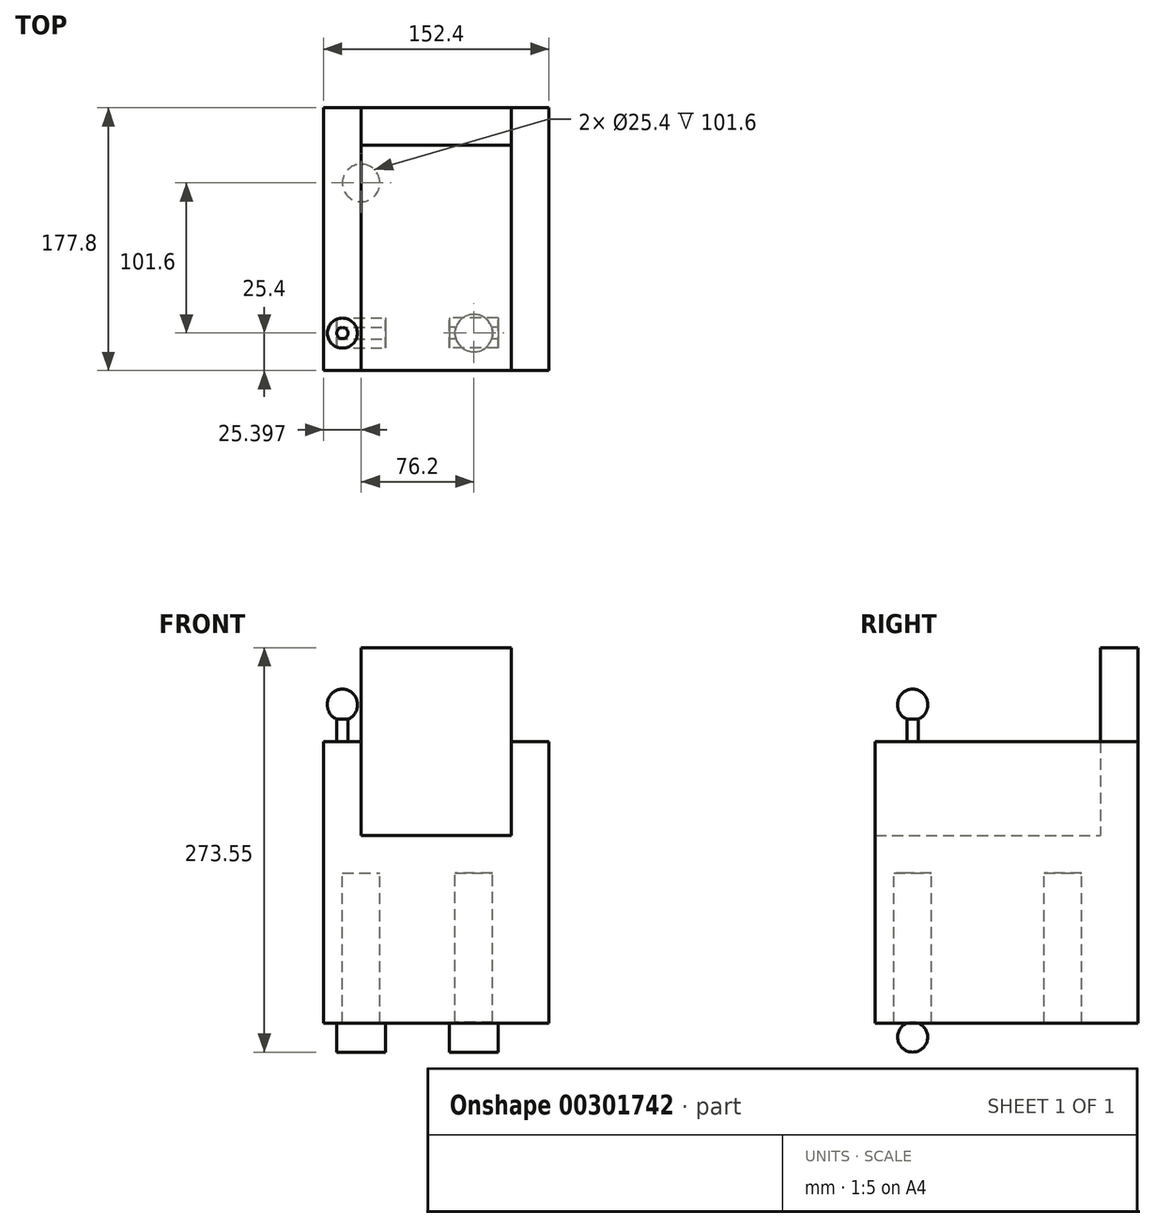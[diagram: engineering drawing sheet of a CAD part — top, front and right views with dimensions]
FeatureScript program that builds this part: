
annotation { "Feature Type Name" : "Feature", "Feature Type Description" : "" }
export const myFeature = defineFeature(function(context is Context, id is Id, definition is map)
    precondition{}
    {
        {
            var Q0;
            Q0=qCreatedBy(makeId("Front.planeOp"),FACE);
            var sketch = newSketch(context, id + "F0", { "sketchPlane" : qUnion([Q0])});
            skLineSegment(sketch, "E0.bottom", {"start": v(-64.76, 10.66) * mm, "end": v(62.24, 10.66) * mm});
            skLineSegment(sketch, "E0.top", {"start": v(-64.76, -14.74) * mm, "end": v(62.24, -14.74) * mm});
            skLineSegment(sketch, "E0.left", {"start": v(-64.76, 10.66) * mm, "end": v(-64.76, -14.74) * mm});
            skLineSegment(sketch, "E0.right", {"start": v(62.24, 10.66) * mm, "end": v(62.24, -14.74) * mm});
            skSolve(sketch);
        }
        {
            var Q0;
            Q0=makeQuery(id+"F0.imprint","IMPRINT",FACE,{"disambiguationData":[TD([[makeQuery(id+"F0.imprint","IMPRINT",EDGE,{"derivedFrom":sQuery(id+"F0.wireOp",EDGE,"E0.bottom")}),-1.0]])]});
            extrude(context, id + "F1", {"entities" : qUnion([Q0]), "endBound" : BoundingType.SYMMETRIC, "depth" : 152.4 * mm});
        }
        {
            var Q0;
            Q0=makeQuery(id+"F1.opExtrude","SWEPT_FACE",FACE,{"disambiguationData":[OSD([sQuery(id+"F0.wireOp",EDGE,"E0.top")])]});
            var sketch = newSketch(context, id + "F2", { "sketchPlane" : qUnion([Q0])});
            skCircle(sketch, "E1", {"center": v(-39.36, 50.8) * mm, "radius": 12.7 * mm});
            skLineSegment(sketch, "E2", {"start": v(-1.26, 76.2) * mm, "end": v(-1.26, -76.2) * mm, "construction": true});
            skLineSegment(sketch, "E3", {"start": v(-64.76, 0) * mm, "end": v(62.24, 0) * mm, "construction": true});
            skCircle(sketch, "E4.MirrorC", {"center": v(36.84, 50.8) * mm, "radius": 12.7 * mm});
            skLineSegment(sketch, "E5.MirrorCS", {"start": v(62.24, 0) * mm, "end": v(-64.76, 0) * mm, "construction": true});
            skCircle(sketch, "E6.MirrorC", {"center": v(-39.36, -50.8) * mm, "radius": 12.7 * mm});
            skCircle(sketch, "E7.MirrorC", {"center": v(36.84, -50.8) * mm, "radius": 12.7 * mm});
            skSolve(sketch);
        }
        {
            var Q0;
            Q0=makeQuery(id+"F2.imprint","IMPRINT",FACE,{"disambiguationData":[TD([[makeQuery(id+"F2.imprint","IMPRINT",EDGE,{"derivedFrom":sQuery(id+"F2.wireOp",EDGE,"E1")}),1.0]])]});
            var Q1;
            Q1=makeQuery(id+"F2.imprint","IMPRINT",FACE,{"disambiguationData":[TD([[makeQuery(id+"F2.imprint","IMPRINT",EDGE,{"derivedFrom":sQuery(id+"F2.wireOp",EDGE,"E4.MirrorC")}),-1.0]])]});
            var Q2;
            Q2=makeQuery(id+"F2.imprint","IMPRINT",FACE,{"disambiguationData":[TD([[makeQuery(id+"F2.imprint","IMPRINT",EDGE,{"derivedFrom":sQuery(id+"F2.wireOp",EDGE,"E7.MirrorC")}),1.0]])]});
            var Q3;
            Q3=makeQuery(id+"F2.imprint","IMPRINT",FACE,{"disambiguationData":[TD([[makeQuery(id+"F2.imprint","IMPRINT",EDGE,{"derivedFrom":sQuery(id+"F2.wireOp",EDGE,"E6.MirrorC")}),-1.0]])]});
            extrude(context, id + "F3", {"entities" : qUnion([Q0, Q1, Q2, Q3]), "operationType" : NewBodyOperationType.ADD, "depth" : 101.6 * mm});
        }
        {
            var Q0;
            Q0=qCreatedBy(makeId("Right.planeOp"),FACE);
            var sketch = newSketch(context, id + "F4", { "sketchPlane" : qUnion([Q0])});
            skCircle(sketch, "E8", {"center": v(-50.8, -125.73) * mm, "radius": 10.16 * mm});
            skLineSegment(sketch, "E9", {"start": v(0, 0) * mm, "end": v(0, -174.12) * mm, "construction": true});
            skCircle(sketch, "E10.MirrorC", {"center": v(50.8, -125.73) * mm, "radius": 10.16 * mm});
            skSolve(sketch);
        }
        {
            var Q0;
            Q0=makeQuery(id+"F4.imprint","IMPRINT",FACE,{"disambiguationData":[TD([[makeQuery(id+"F4.imprint","IMPRINT",EDGE,{"derivedFrom":sQuery(id+"F4.wireOp",EDGE,"E8")}),1.0]])]});
            var Q1;
            Q1=makeQuery(id+"F4.imprint","IMPRINT",FACE,{"disambiguationData":[TD([[makeQuery(id+"F4.imprint","IMPRINT",EDGE,{"derivedFrom":sQuery(id+"F4.wireOp",EDGE,"E10.MirrorC")}),-1.0]])]});
            extrude(context, id + "F5", {"entities" : qUnion([Q0, Q1]), "operationType" : NewBodyOperationType.ADD, "depth" : 53.34 * mm, "hasSecondDirection" : true, "secondDirectionOppositeDirection" : false, "secondDirectionDepth" : 20.32 * mm});
        }
        {
            var Q0;
            Q0=makeQuery(id+"F5.opExtrude","CAP_FACE",FACE,{"disambiguationData":[OSD([sQuery(id+"F4.wireOp",EDGE,"E10.MirrorC")])],"isStart":true});
            var Q1;
            Q1=makeQuery(id+"F5.opExtrude","CAP_FACE",FACE,{"disambiguationData":[OSD([sQuery(id+"F4.wireOp",EDGE,"E8")])],"isStart":true});
            extrude(context, id + "F6", {"entities" : qUnion([Q0, Q1]), "operationType" : NewBodyOperationType.ADD, "depth" : 76.2 * mm, "hasSecondDirection" : true, "secondDirectionOppositeDirection" : false, "secondDirectionDepth" : 43.18 * mm});
        }
        {
            var Q0;
            Q0=makeQuery(id+"F1.opExtrude","SWEPT_FACE",FACE,{"disambiguationData":[OSD([sQuery(id+"F0.wireOp",EDGE,"E0.right")])]});
            extrude(context, id + "F7", {"entities" : qUnion([Q0]), "operationType" : NewBodyOperationType.ADD, "depth" : 25.4 * mm});
        }
        {
            var Q0;
            {var subQ0=sQuery(id+"F0.wireOp",EDGE,"E0.bottom");Q0=makeQuery(id+"F7.boolean.opBoolean","MERGE",FACE,{"derivedFrom":[makeQuery(id+"F1.opExtrude","SWEPT_FACE",FACE,{"disambiguationData":[OSD([subQ0])]}),makeQuery(id+"F7.opExtrude","SWEPT_FACE",FACE,{"disambiguationData":[OSD([subQ0,sQuery(id+"F0.wireOp",EDGE,"E0.right")])]})]});}
            var sketch = newSketch(context, id + "F8", { "sketchPlane" : qUnion([Q0])});
            skLineSegment(sketch, "E11", {"start": v(62.24, -76.2) * mm, "end": v(62.24, 76.2) * mm});
            skLineSegment(sketch, "E12", {"start": v(11.44, -76.2) * mm, "end": v(11.44, 76.2) * mm, "construction": true});
            skLineSegment(sketch, "E13.MirrorCS", {"start": v(-39.36, -76.2) * mm, "end": v(-39.36, 76.2) * mm});
            skSolve(sketch);
        }
        {
            var Q0;
            {var subQ0=sQuery(id+"F8.wireOp",EDGE,"E11");Q0=makeQuery(id+"F8.imprint","IMPRINT",FACE,{"disambiguationData":[TD([[makeQuery(id+"F8.imprint","IMPRINT",EDGE,{"derivedFrom":subQ0}),-1.0]])]});}
            var Q1;
            {var subQ0=sQuery(id+"F8.wireOp",EDGE,"E13.MirrorCS");Q1=makeQuery(id+"F8.imprint","IMPRINT",FACE,{"disambiguationData":[TD([[makeQuery(id+"F8.imprint","IMPRINT",EDGE,{"derivedFrom":subQ0}),1.0]])]});}
            extrude(context, id + "F9", {"entities" : qUnion([Q0, Q1]), "operationType" : NewBodyOperationType.ADD, "depth" : 63.5 * mm});
        }
        {
            var Q0;
            {var subQ0=sQuery(id+"F0.wireOp",EDGE,"E0.right");var subQ1=sQuery(id+"F0.wireOp",EDGE,"E0.bottom");var subQ2=makeQuery(id+"F7.boolean.opBoolean","MERGE",EDGE,{"derivedFrom":[makeQuery(id+"F1.opExtrude","CAP_EDGE",EDGE,{"disambiguationData":[OSD([subQ1])],"isStart":true}),makeQuery(id+"F7.opExtrude","SWEPT_EDGE",EDGE,{"disambiguationData":[OSD([subQ1,subQ0]),TDD([makeQuery(id+"F1.opExtrude","CAP_VERTEX",VERTEX,{"disambiguationData":[OSD([subQ1,subQ0])],"isStart":true})])]})]});var subQ3=sQuery(id+"F0.wireOp",EDGE,"E0.left");Q0=makeQuery(id+"F9.boolean.opBoolean","MERGE",FACE,{"derivedFrom":[makeQuery(id+"F7.boolean.opBoolean","MERGE",FACE,{"derivedFrom":[makeQuery(id+"F1.opExtrude","CAP_FACE",FACE,{"disambiguationData":[OSD([subQ1,sQuery(id+"F0.wireOp",EDGE,"E0.top"),subQ3,subQ0])],"isStart":true}),makeQuery(id+"F7.opExtrude","SWEPT_FACE",FACE,{"disambiguationData":[OSD([subQ0]),TDD([makeQuery(id+"F1.opExtrude","CAP_EDGE",EDGE,{"disambiguationData":[OSD([subQ0])],"isStart":true})])]})]}),makeQuery(id+"F9.opExtrude","SWEPT_FACE",FACE,{"disambiguationData":[OSD([subQ1,subQ0]),TDD([makeQuery(id+"F8.imprint","IMPRINT",EDGE,{"disambiguationData":[TD([[makeQuery(id+"F8.imprint","INTERSECT",VERTEX,{"derivedFrom":[subQ2,sQuery(id+"F8.wireOp",EDGE,"E13.MirrorCS")]}),1.0]])],"derivedFrom":subQ2})])]}),makeQuery(id+"F9.opExtrude","SWEPT_FACE",FACE,{"disambiguationData":[OSD([subQ1,subQ0]),TDD([makeQuery(id+"F8.imprint","IMPRINT",EDGE,{"disambiguationData":[TD([[makeQuery(id+"F8.imprint","INTERSECT",VERTEX,{"derivedFrom":[subQ2,sQuery(id+"F8.wireOp",EDGE,"E11")]}),-1.0]])],"derivedFrom":subQ2})])]})]});}
            extrude(context, id + "F10", {"entities" : qUnion([Q0]), "operationType" : NewBodyOperationType.ADD, "depth" : 25.4 * mm});
        }
        {
            var Q0;
            {var subQ0=sQuery(id+"F0.wireOp",EDGE,"E0.right");var subQ1=sQuery(id+"F0.wireOp",EDGE,"E0.bottom");Q0=makeQuery(id+"F10.boolean.opBoolean","MERGE",FACE,{"derivedFrom":[makeQuery(id+"F7.boolean.opBoolean","MERGE",FACE,{"derivedFrom":[makeQuery(id+"F1.opExtrude","SWEPT_FACE",FACE,{"disambiguationData":[OSD([subQ1])]}),makeQuery(id+"F7.opExtrude","SWEPT_FACE",FACE,{"disambiguationData":[OSD([subQ1,subQ0])]})]}),makeQuery(id+"F10.opExtrude","SWEPT_FACE",FACE,{"disambiguationData":[OSD([subQ1,subQ0]),TDD([makeQuery(id+"F7.boolean.opBoolean","MERGE",EDGE,{"derivedFrom":[makeQuery(id+"F1.opExtrude","CAP_EDGE",EDGE,{"disambiguationData":[OSD([subQ1])],"isStart":true}),makeQuery(id+"F7.opExtrude","SWEPT_EDGE",EDGE,{"disambiguationData":[OSD([subQ1,subQ0]),TDD([makeQuery(id+"F1.opExtrude","CAP_VERTEX",VERTEX,{"disambiguationData":[OSD([subQ1,subQ0])],"isStart":true})])]})]})])]})]});}
            var sketch = newSketch(context, id + "F11", { "sketchPlane" : qUnion([Q0])});
            skLineSegment(sketch, "E14", {"start": v(-39.36, 76.2) * mm, "end": v(62.24, 76.2) * mm});
            skSolve(sketch);
        }
        {
            var Q0;
            Q0 = qSketchRegion(id + "F11", true);
            var Q1;
            {var subQ0=sQuery(id+"F11.wireOp",EDGE,"E14");Q1=makeQuery(id+"F11.imprint","IMPRINT",FACE,{"disambiguationData":[TD([[makeQuery(id+"F11.imprint","IMPRINT",EDGE,{"derivedFrom":subQ0}),1.0]])]});}
            extrude(context, id + "F12", {"entities" : qUnion([Q0, Q1]), "operationType" : NewBodyOperationType.ADD, "depth" : 127 * mm});
        }
        {
            var Q0;
            {var subQ0=sQuery(id+"F0.wireOp",EDGE,"E0.right");var subQ1=sQuery(id+"F0.wireOp",EDGE,"E0.bottom");var subQ2=makeQuery(id+"F7.boolean.opBoolean","MERGE",EDGE,{"derivedFrom":[makeQuery(id+"F1.opExtrude","CAP_EDGE",EDGE,{"disambiguationData":[OSD([subQ1])],"isStart":true}),makeQuery(id+"F7.opExtrude","SWEPT_EDGE",EDGE,{"disambiguationData":[OSD([subQ1,subQ0]),TDD([makeQuery(id+"F1.opExtrude","CAP_VERTEX",VERTEX,{"disambiguationData":[OSD([subQ1,subQ0])],"isStart":true})])]})]});var subQ3=sQuery(id+"F0.wireOp",EDGE,"E0.left");var subQ4=sQuery(id+"F8.wireOp",EDGE,"E13.MirrorCS");Q0=makeQuery(id+"F10.boolean.opBoolean","MERGE",FACE,{"derivedFrom":[makeQuery(id+"F9.opExtrude","CAP_FACE",FACE,{"disambiguationData":[OSD([subQ1,subQ3,subQ0,subQ4])],"isStart":false}),makeQuery(id+"F10.opExtrude","SWEPT_FACE",FACE,{"disambiguationData":[OSD([subQ1,subQ0]),TDD([makeQuery(id+"F9.opExtrude","CAP_EDGE",EDGE,{"disambiguationData":[OSD([subQ1,subQ0]),TDD([makeQuery(id+"F8.imprint","IMPRINT",EDGE,{"disambiguationData":[TD([[makeQuery(id+"F8.imprint","INTERSECT",VERTEX,{"derivedFrom":[subQ2,subQ4]}),1.0]])],"derivedFrom":subQ2})])],"isStart":false})])]})]});}
            var sketch = newSketch(context, id + "F13", { "sketchPlane" : qUnion([Q0])});
            skCircle(sketch, "E15", {"center": v(-52.06, -50.8) * mm, "radius": 3.8 * mm});
            skSolve(sketch);
        }
        {
            var Q0;
            Q0=makeQuery(id+"F13.imprint","IMPRINT",FACE,{"disambiguationData":[TD([[makeQuery(id+"F13.imprint","IMPRINT",EDGE,{"derivedFrom":sQuery(id+"F13.wireOp",EDGE,"E15")}),1.0]])]});
            extrude(context, id + "F14", {"entities" : qUnion([Q0]), "operationType" : NewBodyOperationType.ADD, "depth" : 25.4 * mm});
        }
        {
            var Q0;
            Q0=makeQuery(id+"F14.opExtrude","CAP_FACE",FACE,{"disambiguationData":[OSD([sQuery(id+"F13.wireOp",EDGE,"E15")])],"isStart":false});
            var sketch = newSketch(context, id + "F15", { "sketchPlane" : qUnion([Q0])});
            skCircle(sketch, "E16", {"center": v(-52.06, -50.8) * mm, "radius": 10.16 * mm});
            skSolve(sketch);
        }
        {
            var Q0;
            Q0 = qSketchRegion(id + "F15", true);
            extrude(context, id + "F16", {"entities" : qUnion([Q0]), "operationType" : NewBodyOperationType.ADD, "endBound" : BoundingType.SYMMETRIC, "depth" : 20.32 * mm});
        }
        {
            var Q0;
            Q0=makeQuery(id+"F16.opExtrude","CAP_EDGE",EDGE,{"disambiguationData":[OSD([sQuery(id+"F15.wireOp",EDGE,"E16")])],"isStart":false});
            var Q1;
            Q1=makeQuery(id+"F16.opExtrude","CAP_EDGE",EDGE,{"disambiguationData":[OSD([sQuery(id+"F15.wireOp",EDGE,"E16")])],"isStart":true});
            fillet(context, id + "F17", {"entities" : qUnion([Q0, Q1]), "radius" : 10.16 * mm, "tangentPropagation" : true, "allowEdgeOverflow" : false});
        }
    });
